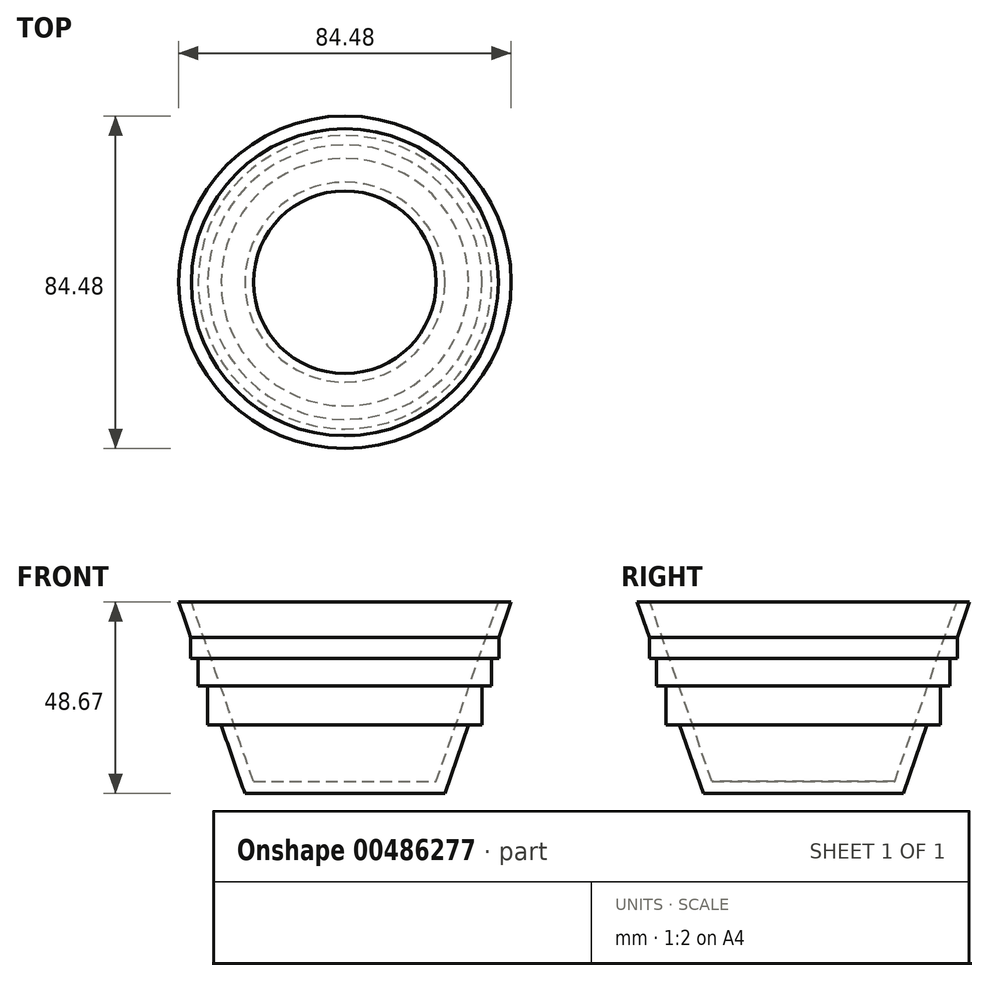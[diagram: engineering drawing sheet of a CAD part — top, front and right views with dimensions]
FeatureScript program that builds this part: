
annotation { "Feature Type Name" : "Feature", "Feature Type Description" : "" }
export const myFeature = defineFeature(function(context is Context, id is Id, definition is map)
    precondition{}
    {
        {
            var Q0;
            Q0=qCreatedBy(makeId("Front.planeOp"),FACE);
            var sketch = newSketch(context, id + "F0", { "sketchPlane" : qUnion([Q0])});
            skLineSegment(sketch, "E0", {"start": v(0, 0) * mm, "end": v(0, 48.67) * mm, "construction": true});
            skLineSegment(sketch, "E1", {"start": v(25.4, 0) * mm, "end": v(42.24, 48.67) * mm});
            skLineSegment(sketch, "E2", {"start": v(0, 0) * mm, "end": v(25.4, 0) * mm});
            skLineSegment(sketch, "E3.0", {"start": v(23.21, 3.07) * mm, "end": v(38.99, 48.67) * mm});
            skLineSegment(sketch, "E3.1", {"start": v(0, 3.07) * mm, "end": v(23.21, 3.07) * mm});
            skLineSegment(sketch, "E4", {"start": v(0, 3.07) * mm, "end": v(0, 0) * mm});
            skLineSegment(sketch, "E5", {"start": v(38.99, 48.67) * mm, "end": v(42.24, 48.67) * mm});
            skLineSegment(sketch, "E6", {"start": v(39.14, 39.71) * mm, "end": v(39.14, 34.34) * mm});
            skLineSegment(sketch, "E7", {"start": v(39.14, 34.34) * mm, "end": v(37.28, 34.34) * mm});
            skLineSegment(sketch, "E8", {"start": v(37.28, 34.34) * mm, "end": v(37.28, 27.36) * mm});
            skLineSegment(sketch, "E9", {"start": v(37.28, 27.36) * mm, "end": v(34.86, 27.36) * mm});
            skLineSegment(sketch, "E10", {"start": v(34.86, 27.36) * mm, "end": v(34.86, 17.42) * mm});
            skLineSegment(sketch, "E11", {"start": v(34.86, 17.42) * mm, "end": v(31.42, 17.42) * mm});
            skSolve(sketch);
        }
        {
            var Q0;
            Q0=makeQuery(id+"F0.imprint","IMPRINT",FACE,{"disambiguationData":[TD([[makeQuery(id+"F0.imprint","IMPRINT",EDGE,{"derivedFrom":sQuery(id+"F0.wireOp",EDGE,"E1")}),1.0]])]});
            var Q1;
            {var subQ0=sQuery(id+"F0.wireOp",EDGE,"E10");Q1=makeQuery(id+"F0.imprint","IMPRINT",FACE,{"disambiguationData":[TD([[makeQuery(id+"F0.imprint","IMPRINT",EDGE,{"derivedFrom":subQ0}),-1.0]])]});}
            var Q2;
            {var subQ0=sQuery(id+"F0.wireOp",EDGE,"E8");Q2=makeQuery(id+"F0.imprint","IMPRINT",FACE,{"disambiguationData":[TD([[makeQuery(id+"F0.imprint","IMPRINT",EDGE,{"derivedFrom":subQ0}),-1.0]])]});}
            var Q3;
            {var subQ0=sQuery(id+"F0.wireOp",EDGE,"E6");Q3=makeQuery(id+"F0.imprint","IMPRINT",FACE,{"disambiguationData":[TD([[makeQuery(id+"F0.imprint","IMPRINT",EDGE,{"derivedFrom":subQ0}),-1.0]])]});}
            var Q4;
            Q4=sQuery(id+"F0.wireOp",EDGE,"E0");
            revolve(context, id + "F1", {"entities" : qUnion([Q0, Q1, Q2, Q3]), "axis" : qUnion([Q4]), "revolveType" : RevolveType.FULL});
        }
    });
